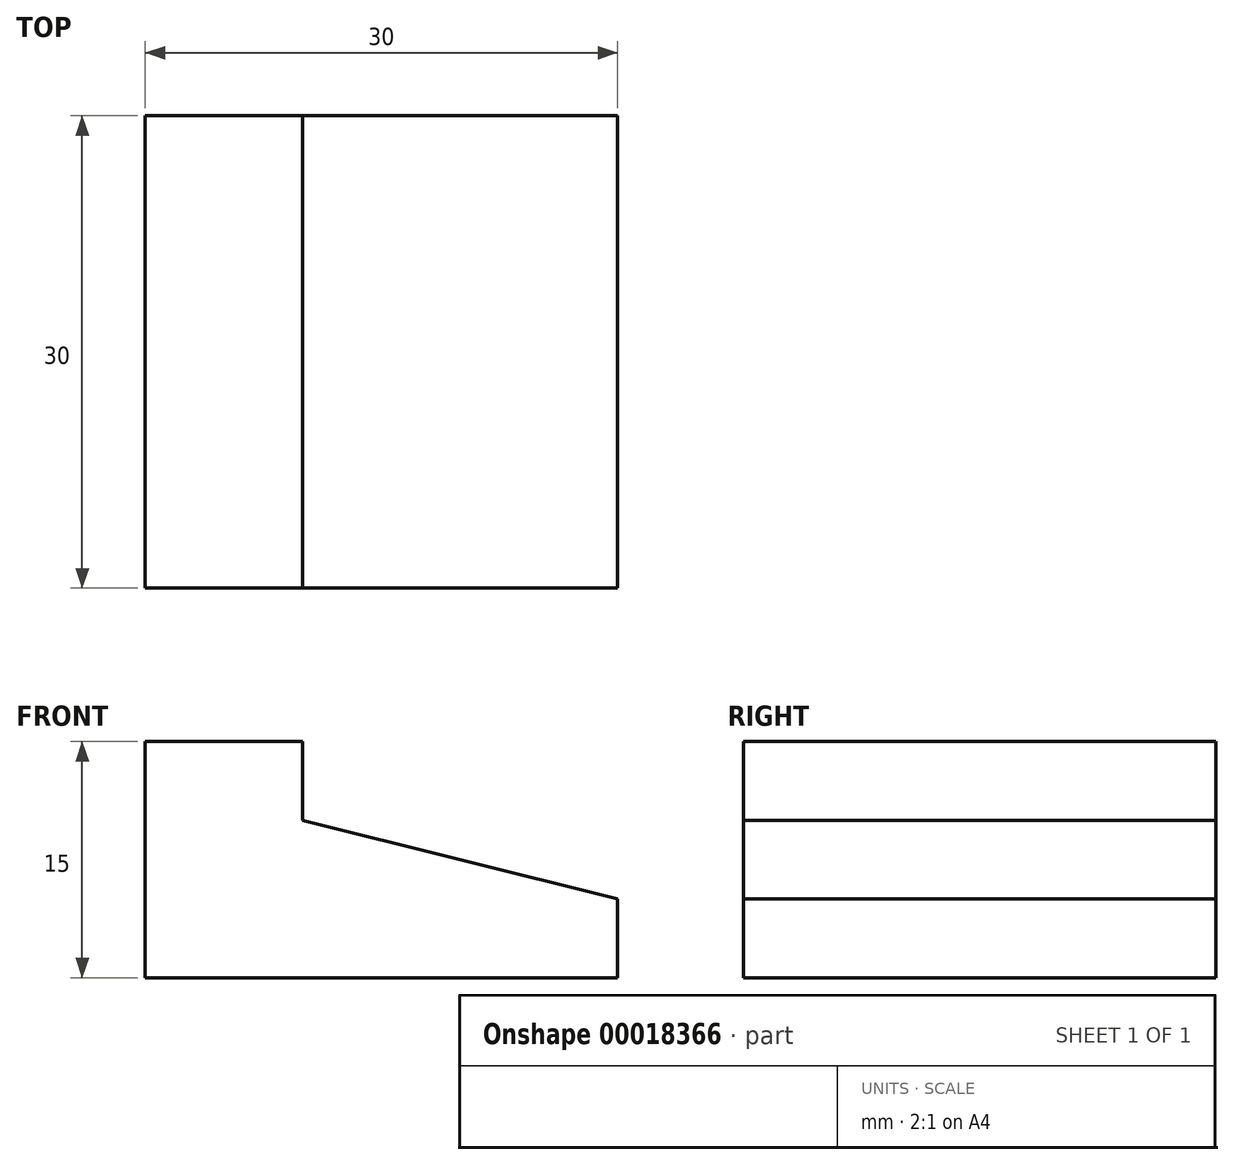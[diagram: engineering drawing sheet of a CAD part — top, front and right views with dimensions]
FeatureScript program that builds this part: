
annotation { "Feature Type Name" : "Feature", "Feature Type Description" : "" }
export const myFeature = defineFeature(function(context is Context, id is Id, definition is map)
    precondition{}
    {
        {
            var Q0;
            Q0=qCreatedBy(makeId("Front.planeOp"),FACE);
            var sketch = newSketch(context, id + "F0", { "sketchPlane" : qUnion([Q0])});
            skLineSegment(sketch, "E0", {"start": v(-30.58, 51.64) * mm, "end": v(-30.58, 36.64) * mm});
            skLineSegment(sketch, "E1", {"start": v(-30.58, 36.64) * mm, "end": v(-0.58, 36.64) * mm});
            skLineSegment(sketch, "E2", {"start": v(-30.58, 51.64) * mm, "end": v(-20.58, 51.64) * mm});
            skLineSegment(sketch, "E3", {"start": v(-20.58, 51.64) * mm, "end": v(-20.58, 46.64) * mm});
            skLineSegment(sketch, "E4", {"start": v(-20.58, 46.64) * mm, "end": v(-0.58, 41.64) * mm});
            skLineSegment(sketch, "E5", {"start": v(-0.58, 41.64) * mm, "end": v(-0.58, 36.64) * mm});
            skSolve(sketch);
        }
        {
            var Q0;
            Q0=makeQuery(id+"F0.imprint","IMPRINT",FACE,{"disambiguationData":[TD([[makeQuery(id+"F0.imprint","IMPRINT",EDGE,{"derivedFrom":sQuery(id+"F0.wireOp",EDGE,"E0")}),1.0]])]});
            extrude(context, id + "F1", {"entities" : qUnion([Q0]), "depth" : 30 * mm});
        }
    });
